# Revit family: Indoor_Pendant Lamp_Santa&Cole_Sexta
name_source: partatom
category: Luminarias
revit_build: Autodesk Revit 2018 (Build: 20190510_1515(x64)
units: mm (PartAtom-declared; Revit-internal decimal feet)

## family parameters
Anfitrión = Cara
Compartido = No
Corte con vacíos al cargar = No
Cota de conector redondo = Diámetro de uso
Origen de luz = No
Punto de cálculo de habitación = No
Tipo de pieza = Normal

## types (2) — shared parameters
Assembly Instructions - CE = https://www.santacole.com
Assembly Instructions - UL = https://www.santacole.com
Elevación por defecto = 1219 mm
Energy Label = https://www.santacole.com
Fabricante = Santa & Cole
Manufacturer website = http://www.santacole.com
Modelo = Sexta
Technical Information = https://www.santacole.com
URL = https://www.santacole.com
Voltaje (90-305 V) = 220 V

## per-type parameters (varying)
| type | Carga aparente | Code | Load | Visibility_Sexta | Visibility_Sexta 12 |
| Sexta | 72 W | SXT41+6SXT03+SXT0x | 72 W | Sí | No |
| Sexta 12 | 144 W | SXT12+6SXT04 | 144 W | No | Sí |

## geometry (parser evidence)
native form markers: Sweep x4
no freeform markers — native parametric forms only
